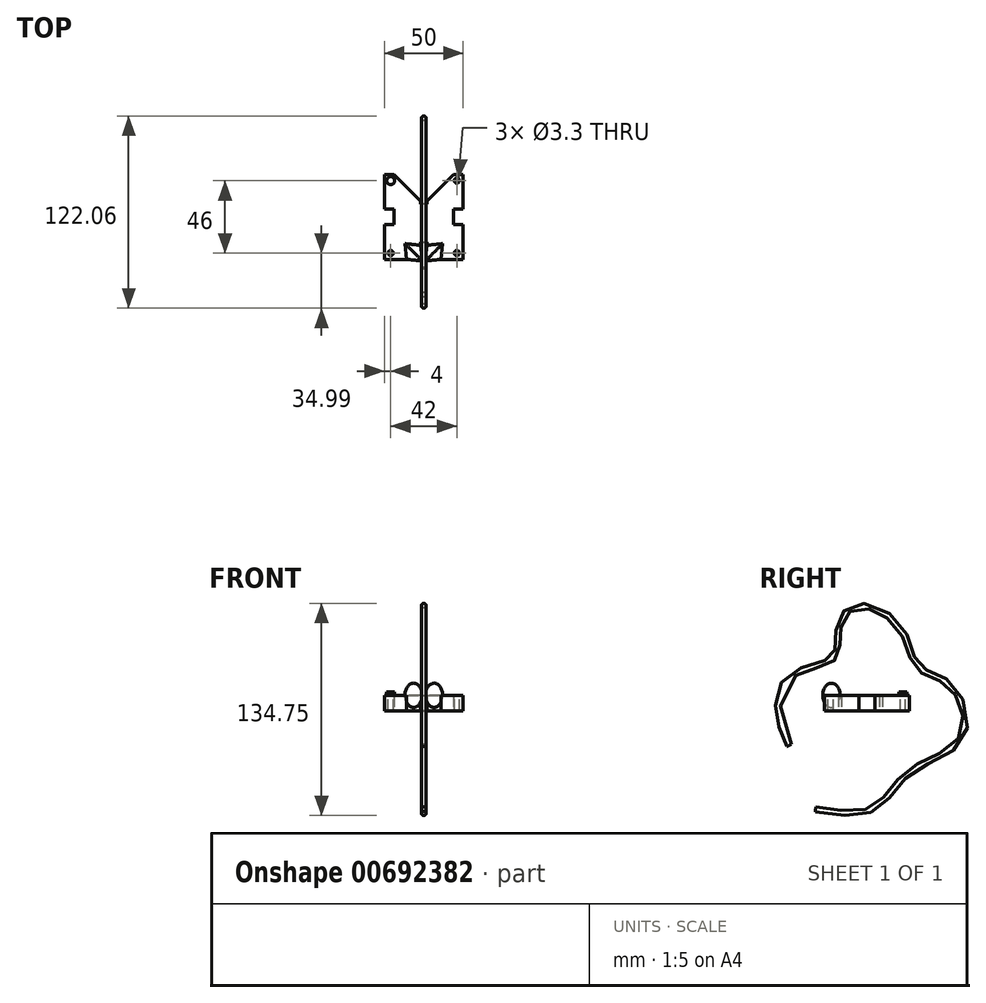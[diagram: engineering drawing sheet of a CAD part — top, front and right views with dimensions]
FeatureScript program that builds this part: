
annotation { "Feature Type Name" : "Feature", "Feature Type Description" : "" }
export const myFeature = defineFeature(function(context is Context, id is Id, definition is map)
    precondition{}
    {
        {
            var Q0;
            Q0=qCreatedBy(makeId("Top.planeOp"),FACE);
            var sketch = newSketch(context, id + "F0", { "sketchPlane" : qUnion([Q0])});
            skLineSegment(sketch, "E0", {"start": v(-2, 10) * mm, "end": v(-19, 27) * mm});
            skLineSegment(sketch, "E1", {"start": v(-19, 27) * mm, "end": v(-25, 27) * mm});
            skLineSegment(sketch, "E2", {"start": v(-25, 27) * mm, "end": v(-25, 5) * mm});
            skLineSegment(sketch, "E3", {"start": v(-25, 5) * mm, "end": v(-19, 5) * mm});
            skLineSegment(sketch, "E4", {"start": v(-19, 5) * mm, "end": v(-19, -5) * mm});
            skLineSegment(sketch, "E5", {"start": v(-19, -5) * mm, "end": v(-25, -5) * mm});
            skLineSegment(sketch, "E6", {"start": v(-25, -5) * mm, "end": v(-25, -27) * mm});
            skLineSegment(sketch, "E7", {"start": v(-25, -27) * mm, "end": v(-11, -27) * mm});
            skLineSegment(sketch, "E8", {"start": v(-11, -27) * mm, "end": v(-2, -18) * mm});
            skLineSegment(sketch, "E9", {"start": v(-2, -18) * mm, "end": v(-2, -16) * mm});
            skLineSegment(sketch, "E10", {"start": v(-2, -16) * mm, "end": v(0, -16) * mm});
            skLineSegment(sketch, "E11", {"start": v(-2, 10) * mm, "end": v(-2, 8) * mm});
            skLineSegment(sketch, "E12", {"start": v(-2, 8) * mm, "end": v(0, 8) * mm});
            skLineSegment(sketch, "E13.MirrorCS", {"start": v(2, 8) * mm, "end": v(0, 8) * mm});
            skLineSegment(sketch, "E14.MirrorCS", {"start": v(2, 10) * mm, "end": v(2, 8) * mm});
            skLineSegment(sketch, "E15.MirrorCS", {"start": v(2, -18) * mm, "end": v(2, -16) * mm});
            skLineSegment(sketch, "E16.MirrorCS", {"start": v(2, -16) * mm, "end": v(0, -16) * mm});
            skLineSegment(sketch, "E17.MirrorCS", {"start": v(25, 5) * mm, "end": v(19, 5) * mm});
            skLineSegment(sketch, "E18.MirrorCS", {"start": v(19, 27) * mm, "end": v(25, 27) * mm});
            skLineSegment(sketch, "E19.MirrorCS", {"start": v(2, 10) * mm, "end": v(19, 27) * mm});
            skLineSegment(sketch, "E20.MirrorCS", {"start": v(25, 27) * mm, "end": v(25, 5) * mm});
            skLineSegment(sketch, "E21.MirrorCS", {"start": v(25, -5) * mm, "end": v(25, -27) * mm});
            skLineSegment(sketch, "E22.MirrorCS", {"start": v(25, -27) * mm, "end": v(11, -27) * mm});
            skLineSegment(sketch, "E23.MirrorCS", {"start": v(19, 5) * mm, "end": v(19, -5) * mm});
            skLineSegment(sketch, "E24.MirrorCS", {"start": v(11, -27) * mm, "end": v(2, -18) * mm});
            skLineSegment(sketch, "E25.MirrorCS", {"start": v(19, -5) * mm, "end": v(25, -5) * mm});
            skSolve(sketch);
        }
        {
            var Q0;
            Q0 = qSketchRegion(id + "F0", true);
            extrude(context, id + "F1", {"entities" : qUnion([Q0]), "depth" : 10 * mm, "offsetDistance" : 25 * mm});
        }
        {
            var Q0;
            Q0=makeQuery(id+"F1.opExtrude","CAP_FACE",FACE,{"disambiguationData":[OSD([sQuery(id+"F0.wireOp",EDGE,"E0"),sQuery(id+"F0.wireOp",EDGE,"E1"),sQuery(id+"F0.wireOp",EDGE,"E2"),sQuery(id+"F0.wireOp",EDGE,"E3"),sQuery(id+"F0.wireOp",EDGE,"E4"),sQuery(id+"F0.wireOp",EDGE,"E5"),sQuery(id+"F0.wireOp",EDGE,"E6"),sQuery(id+"F0.wireOp",EDGE,"E7"),sQuery(id+"F0.wireOp",EDGE,"E8"),sQuery(id+"F0.wireOp",EDGE,"E9"),sQuery(id+"F0.wireOp",EDGE,"E10"),sQuery(id+"F0.wireOp",EDGE,"E11"),sQuery(id+"F0.wireOp",EDGE,"E12"),sQuery(id+"F0.wireOp",EDGE,"E13.MirrorCS"),sQuery(id+"F0.wireOp",EDGE,"E14.MirrorCS"),sQuery(id+"F0.wireOp",EDGE,"E15.MirrorCS"),sQuery(id+"F0.wireOp",EDGE,"E16.MirrorCS"),sQuery(id+"F0.wireOp",EDGE,"E17.MirrorCS"),sQuery(id+"F0.wireOp",EDGE,"E18.MirrorCS"),sQuery(id+"F0.wireOp",EDGE,"E19.MirrorCS"),sQuery(id+"F0.wireOp",EDGE,"E20.MirrorCS"),sQuery(id+"F0.wireOp",EDGE,"E21.MirrorCS"),sQuery(id+"F0.wireOp",EDGE,"E22.MirrorCS"),sQuery(id+"F0.wireOp",EDGE,"E23.MirrorCS"),sQuery(id+"F0.wireOp",EDGE,"E24.MirrorCS"),sQuery(id+"F0.wireOp",EDGE,"E25.MirrorCS")])],"isStart":false});
            var sketch = newSketch(context, id + "F2", { "sketchPlane" : qUnion([Q0])});
            skPoint(sketch, "E26", {"position": v(-21, -23) * mm});
            skPoint(sketch, "E27.0.1.0", {"position": v(-21, 23) * mm});
            skPoint(sketch, "E27.1.0.0", {"position": v(21, -23) * mm});
            skPoint(sketch, "E27.1.1.0", {"position": v(21, 23) * mm});
            skLineSegment(sketch, "E27.direction1", {"start": v(-21, -23) * mm, "end": v(21, -23) * mm, "construction": true});
            skLineSegment(sketch, "E27.direction2", {"start": v(-21, -23) * mm, "end": v(-21, 23) * mm, "construction": true});
            skSolve(sketch);
        }
        {
            var Q0;
            Q0=sQuery(id+"F2.wireOp",VERTEX,"E26");
            var Q1;
            Q1=sQuery(id+"F2.wireOp",VERTEX,"E27.1.0.0");
            var Q2;
            Q2=sQuery(id+"F2.wireOp",VERTEX,"E27.1.1.0");
            var Q3;
            Q3=sQuery(id+"F2.wireOp",VERTEX,"E27.0.1.0");
            var Q4;
            Q4=makeQuery(id+"F1.opExtrude","SWEPT_BODY",BODY,{"disambiguationData":[OSD([sQuery(id+"F0.wireOp",EDGE,"E0"),sQuery(id+"F0.wireOp",EDGE,"E1"),sQuery(id+"F0.wireOp",EDGE,"E2"),sQuery(id+"F0.wireOp",EDGE,"E3"),sQuery(id+"F0.wireOp",EDGE,"E4"),sQuery(id+"F0.wireOp",EDGE,"E5"),sQuery(id+"F0.wireOp",EDGE,"E6"),sQuery(id+"F0.wireOp",EDGE,"E7"),sQuery(id+"F0.wireOp",EDGE,"E8"),sQuery(id+"F0.wireOp",EDGE,"E9"),sQuery(id+"F0.wireOp",EDGE,"E10"),sQuery(id+"F0.wireOp",EDGE,"E11"),sQuery(id+"F0.wireOp",EDGE,"E12"),sQuery(id+"F0.wireOp",EDGE,"E13.MirrorCS"),sQuery(id+"F0.wireOp",EDGE,"E14.MirrorCS"),sQuery(id+"F0.wireOp",EDGE,"E15.MirrorCS"),sQuery(id+"F0.wireOp",EDGE,"E16.MirrorCS"),sQuery(id+"F0.wireOp",EDGE,"E17.MirrorCS"),sQuery(id+"F0.wireOp",EDGE,"E18.MirrorCS"),sQuery(id+"F0.wireOp",EDGE,"E19.MirrorCS"),sQuery(id+"F0.wireOp",EDGE,"E20.MirrorCS"),sQuery(id+"F0.wireOp",EDGE,"E21.MirrorCS"),sQuery(id+"F0.wireOp",EDGE,"E22.MirrorCS"),sQuery(id+"F0.wireOp",EDGE,"E23.MirrorCS"),sQuery(id+"F0.wireOp",EDGE,"E24.MirrorCS"),sQuery(id+"F0.wireOp",EDGE,"E25.MirrorCS")])]});
            hole(context, id + "F3", {"style" : HoleStyle.SIMPLE, "endStyle" : HoleEndStyle.BLIND, "standardTappedOrClearance" : lookupTablePath({ "standard" : "ISO", "fit" : "Normal", "size" : "M3", "type" : "Clearance" }), "standardBlindInLast" : lookupTablePath({ "fit" : "Standard", "standard" : "ISO", "size" : "M3", "type" : "Clearance" }), "holeDiameter" : 3.3 * mm, "majorDiameter" : 5 * mm, "holeDepth" : 13.5 * mm, "isTappedThrough" : true, "tappedDepth" : 12 * mm, "tapClearance" : 3, "locations" : qUnion([Q0, Q1, Q2, Q3]), "scope" : qUnion([Q4])});
        }
        {
            var Q0;
            Q0=makeQuery(id+"F1.opExtrude","CAP_FACE",FACE,{"disambiguationData":[OSD([sQuery(id+"F0.wireOp",EDGE,"E0"),sQuery(id+"F0.wireOp",EDGE,"E1"),sQuery(id+"F0.wireOp",EDGE,"E2"),sQuery(id+"F0.wireOp",EDGE,"E3"),sQuery(id+"F0.wireOp",EDGE,"E4"),sQuery(id+"F0.wireOp",EDGE,"E5"),sQuery(id+"F0.wireOp",EDGE,"E6"),sQuery(id+"F0.wireOp",EDGE,"E7"),sQuery(id+"F0.wireOp",EDGE,"E8"),sQuery(id+"F0.wireOp",EDGE,"E9"),sQuery(id+"F0.wireOp",EDGE,"E10"),sQuery(id+"F0.wireOp",EDGE,"E11"),sQuery(id+"F0.wireOp",EDGE,"E12"),sQuery(id+"F0.wireOp",EDGE,"E13.MirrorCS"),sQuery(id+"F0.wireOp",EDGE,"E14.MirrorCS"),sQuery(id+"F0.wireOp",EDGE,"E15.MirrorCS"),sQuery(id+"F0.wireOp",EDGE,"E16.MirrorCS"),sQuery(id+"F0.wireOp",EDGE,"E17.MirrorCS"),sQuery(id+"F0.wireOp",EDGE,"E18.MirrorCS"),sQuery(id+"F0.wireOp",EDGE,"E19.MirrorCS"),sQuery(id+"F0.wireOp",EDGE,"E20.MirrorCS"),sQuery(id+"F0.wireOp",EDGE,"E21.MirrorCS"),sQuery(id+"F0.wireOp",EDGE,"E22.MirrorCS"),sQuery(id+"F0.wireOp",EDGE,"E23.MirrorCS"),sQuery(id+"F0.wireOp",EDGE,"E24.MirrorCS"),sQuery(id+"F0.wireOp",EDGE,"E25.MirrorCS")])],"isStart":false});
            var sketch = newSketch(context, id + "F4", { "sketchPlane" : qUnion([Q0])});
            skCircle(sketch, "E28.0", {"center": v(-21, 23) * mm, "radius": 1.65 * mm});
            skSolve(sketch);
        }
        {
            var Q0;
            Q0 = qSketchRegion(id + "F4", true);
            var Q1;
            Q1=makeQuery(id+"F1.opExtrude","CAP_FACE",FACE,{"disambiguationData":[OSD([sQuery(id+"F0.wireOp",EDGE,"E0"),sQuery(id+"F0.wireOp",EDGE,"E1"),sQuery(id+"F0.wireOp",EDGE,"E2"),sQuery(id+"F0.wireOp",EDGE,"E3"),sQuery(id+"F0.wireOp",EDGE,"E4"),sQuery(id+"F0.wireOp",EDGE,"E5"),sQuery(id+"F0.wireOp",EDGE,"E6"),sQuery(id+"F0.wireOp",EDGE,"E7"),sQuery(id+"F0.wireOp",EDGE,"E8"),sQuery(id+"F0.wireOp",EDGE,"E9"),sQuery(id+"F0.wireOp",EDGE,"E10"),sQuery(id+"F0.wireOp",EDGE,"E11"),sQuery(id+"F0.wireOp",EDGE,"E12"),sQuery(id+"F0.wireOp",EDGE,"E13.MirrorCS"),sQuery(id+"F0.wireOp",EDGE,"E14.MirrorCS"),sQuery(id+"F0.wireOp",EDGE,"E15.MirrorCS"),sQuery(id+"F0.wireOp",EDGE,"E16.MirrorCS"),sQuery(id+"F0.wireOp",EDGE,"E17.MirrorCS"),sQuery(id+"F0.wireOp",EDGE,"E18.MirrorCS"),sQuery(id+"F0.wireOp",EDGE,"E19.MirrorCS"),sQuery(id+"F0.wireOp",EDGE,"E20.MirrorCS"),sQuery(id+"F0.wireOp",EDGE,"E21.MirrorCS"),sQuery(id+"F0.wireOp",EDGE,"E22.MirrorCS"),sQuery(id+"F0.wireOp",EDGE,"E23.MirrorCS"),sQuery(id+"F0.wireOp",EDGE,"E24.MirrorCS"),sQuery(id+"F0.wireOp",EDGE,"E25.MirrorCS")])],"isStart":true});
            extrude(context, id + "F5", {"entities" : qUnion([Q0]), "depth" : 2 * mm, "offsetDistance" : 25 * mm, "hasSecondDirection" : true, "secondDirectionBound" : SecondDirectionBoundingType.UP_TO_SURFACE, "secondDirectionOppositeDirection" : true, "secondDirectionDepth" : 25 * mm, "secondDirectionBoundEntityFace" : qUnion([Q1])});
        }
        {
            var Q0;
            Q0=makeQuery(id+"F5.opExtrude","CAP_FACE",FACE,{"disambiguationData":[OSD([sQuery(id+"F4.wireOp",EDGE,"E28.0")])],"isStart":false});
            var sketch = newSketch(context, id + "F6", { "sketchPlane" : qUnion([Q0])});
            skCircle(sketch, "E29", {"center": v(-21, 23) * mm, "radius": 2.53 * mm});
            skSolve(sketch);
        }
        {
            var Q0;
            Q0 = qSketchRegion(id + "F6", true);
            extrude(context, id + "F7", {"entities" : qUnion([Q0]), "operationType" : NewBodyOperationType.ADD, "oppositeDirection" : true, "depth" : 2 * mm, "offsetDistance" : 25 * mm});
        }
        {
            var Q0;
            Q0=makeQuery(id+"F1.opExtrude","CAP_EDGE",EDGE,{"disambiguationData":[OSD([sQuery(id+"F0.wireOp",EDGE,"E24.MirrorCS")])],"isStart":false});
            var Q1;
            Q1=qCreatedBy(makeId("Top.planeOp"),FACE);
            cPlane(context, id + "F8", {"entities" : qUnion([Q0, Q1]), "cplaneType" : CPlaneType.LINE_ANGLE, "offset" : 25 * mm, "angle" : 45 * degree, "width" : 150 * mm, "height" : 150 * mm});
        }
        {
            var Q0;
            Q0=qCreatedBy(id+"F8.planeOp",FACE);
            var sketch = newSketch(context, id + "F9", { "sketchPlane" : qUnion([Q0])});
            skLineSegment(sketch, "E30.0", {"start": v(13.24, 27.82) * mm, "end": v(2.85, 20.47) * mm});
            skLineSegment(sketch, "E31", {"start": v(2.85, 20.47) * mm, "end": v(3.59, 30.44) * mm});
            skLineSegment(sketch, "E32", {"start": v(3.59, 30.44) * mm, "end": v(13.24, 27.82) * mm});
            skSolve(sketch);
        }
        {
            var Q0;
            Q0=makeQuery(id+"F9.imprint","IMPRINT",FACE,{"disambiguationData":[TD([[makeQuery(id+"F9.imprint","IMPRINT",EDGE,{"derivedFrom":sQuery(id+"F9.wireOp",EDGE,"E30.0")}),-1.0]])]});
            var Q1;
            Q1=sQuery(id+"F9.wireOp",EDGE,"E30.0");
            revolve(context, id + "F10", {"entities" : qUnion([Q0]), "axis" : qUnion([Q1]), "revolveType" : RevolveType.FULL});
        }
        {
            var Q0;
            Q0=makeQuery(id+"F10.opRevolve","SWEPT_BODY",BODY,{"disambiguationData":[OSD([sQuery(id+"F9.wireOp",EDGE,"E30.0"),sQuery(id+"F9.wireOp",EDGE,"E31"),sQuery(id+"F9.wireOp",EDGE,"E32")])]});
            var Q1;
            Q1=qCreatedBy(makeId("Right.planeOp"),FACE);
            mirror(context, id + "F11", {"entities" : qUnion([Q0]), "mirrorPlane" : qUnion([Q1])});
        }
        {
            var Q0;
            Q0=qCreatedBy(makeId("Right.planeOp"),FACE);
            var sketch = newSketch(context, id + "F12", { "sketchPlane" : qUnion([Q0])});
            skFitSpline(sketch, "E33", {"points": [v(-49.33, -21.81) * mm, v(-56.38, 0) * mm, v(-47.63, 22.93) * mm, v(-21.12, 33.62) * mm, v(-18.2, 51.13) * mm, v(-7.5, 66.45) * mm, v(20.94, 53.32) * mm, v(32.37, 28.03) * mm, v(53.52, 16.12) * mm, v(60.08, -17.2) * mm, v(26.77, -38.83) * mm, v(4.9, -61.69) * mm, v(-32.55, -62.42) * mm], "startDerivative": vector(-127.51, 273.13) * mm, "endDerivative": vector(-439.18, 68.8) * mm});
            skSolve(sketch);
        }
        {
            var Q0;
            Q0=sQuery(id+"F12.wireOp",VERTEX,"E33.0.internal");
            var Q1;
            Q1=sQuery(id+"F12.wireOp",EDGE,"E33");
            cPlane(context, id + "F13", {"entities" : qUnion([Q0, Q1]), "cplaneType" : CPlaneType.CURVE_POINT, "offset" : 25 * mm, "width" : 150 * mm, "height" : 150 * mm});
        }
        {
            var Q0;
            Q0=qCreatedBy(id+"F13.planeOp",FACE);
            var sketch = newSketch(context, id + "F14", { "sketchPlane" : qUnion([Q0])});
            skPoint(sketch, "E34.0", {"position": v(0, -53.92) * mm});
            skCircle(sketch, "E35", {"center": v(0, -53.92) * mm, "radius": 1.5 * mm});
            skSolve(sketch);
        }
        {
            var Q0;
            Q0=makeQuery(id+"F14.imprint","IMPRINT",FACE,{"disambiguationData":[TD([[makeQuery(id+"F14.imprint","IMPRINT",EDGE,{"derivedFrom":sQuery(id+"F14.wireOp",EDGE,"E35")}),1.0]])]});
            var Q1;
            Q1=sQuery(id+"F12.wireOp",EDGE,"E33");
            sweep(context, id + "F15", {"profiles" : qUnion([Q0]), "path" : qUnion([Q1])});
        }
    });
